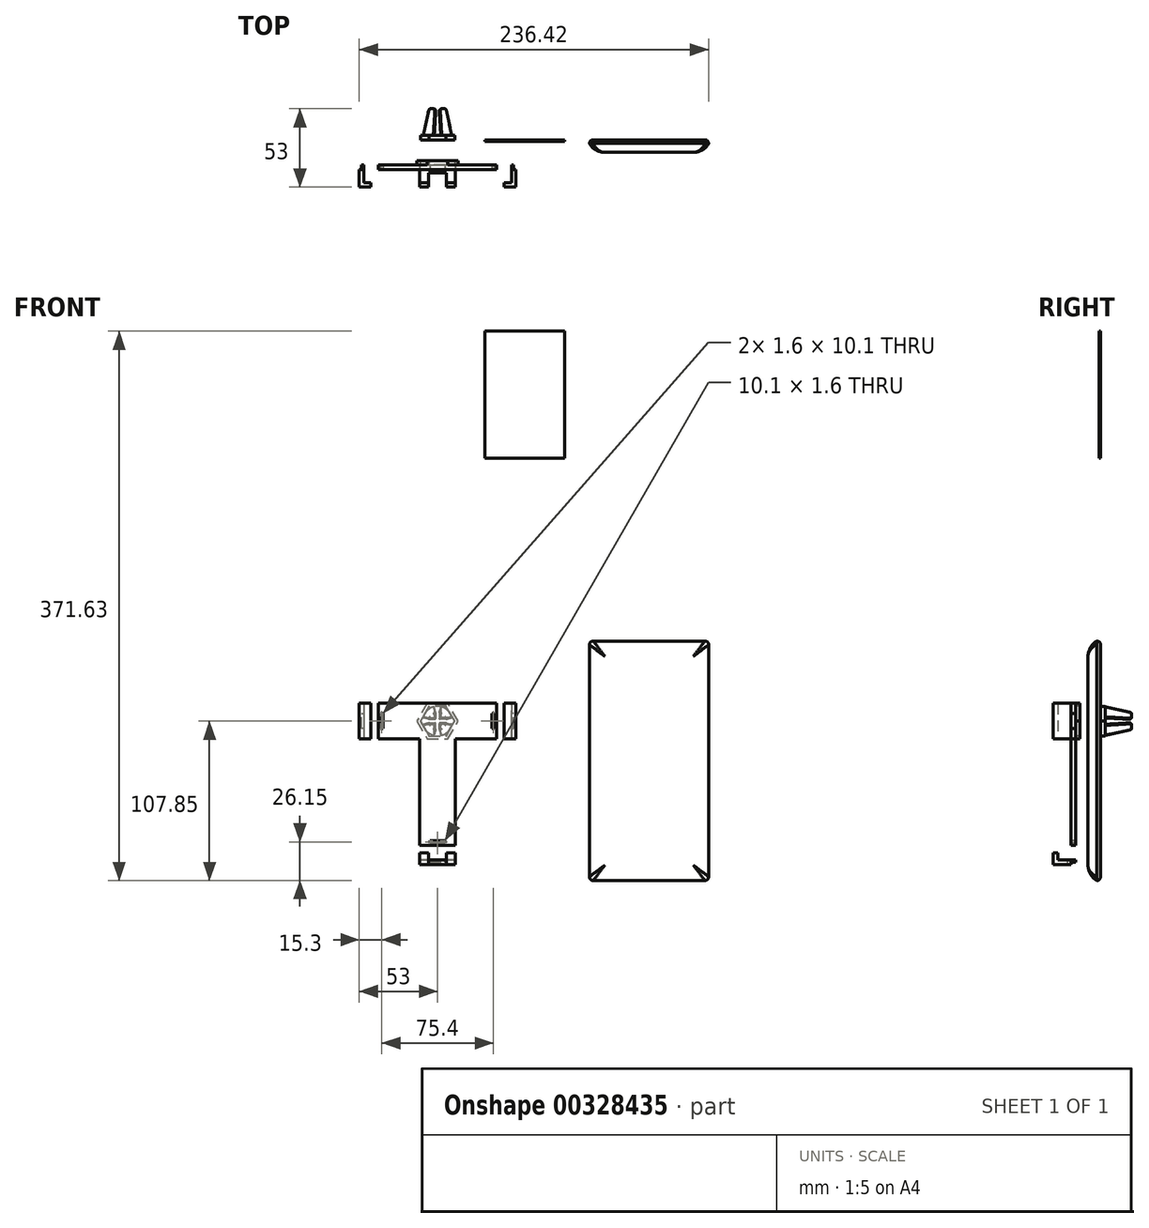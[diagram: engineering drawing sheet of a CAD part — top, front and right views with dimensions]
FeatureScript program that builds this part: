
annotation { "Feature Type Name" : "Feature", "Feature Type Description" : "" }
export const myFeature = defineFeature(function(context is Context, id is Id, definition is map)
    precondition{}
    {
        {
            assignVariable(context, id + "F0", {"name" : "depth_phone", "anyValue" : 8.5});
        }
        {
            var Q0;
            Q0=qCreatedBy(makeId("Front.planeOp"),FACE);
            var sketch = newSketch(context, id + "F1", { "sketchPlane" : qUnion([Q0])});
            skCircle(sketch, "E0", {"center": v(0, 0) * mm, "radius": 10 * mm});
            skSolve(sketch);
        }
        {
            var Q0;
            Q0=qSketchRegion(id+"F1",true);
            extrude(context, id + "F2", {"entities" : qUnion([Q0]), "oppositeDirection" : true, "depth" : 3 * mm});
        }
        {
            var Q0;
            Q0=makeQuery(id+"F2.opExtrude","CAP_FACE",FACE,{"disambiguationData":[OSD([sQuery(id+"F1.wireOp",EDGE,"E0")])],"isStart":false});
            var sketch = newSketch(context, id + "F3", { "sketchPlane" : qUnion([Q0])});
            skLineSegment(sketch, "E1.top", {"start": v(-9.75, 2.2) * mm, "end": v(-2.2, 2.2) * mm});
            skLineSegment(sketch, "E1.right", {"start": v(-2.2, 9.75) * mm, "end": v(-2.2, 2.2) * mm});
            skArc(sketch, "E2", {"start": v(-2.2, 9.75) * mm, "mid": v(-7.07, 7.07) * mm, "end": v(-9.75, 2.2) * mm});
            skLineSegment(sketch, "E3.1.0", {"start": v(-9.75, -2.2) * mm, "end": v(-2.2, -2.2) * mm});
            skLineSegment(sketch, "E3.1.1", {"start": v(-2.2, -9.75) * mm, "end": v(-2.2, -2.2) * mm});
            skArc(sketch, "E3.1.2", {"start": v(-9.75, -2.2) * mm, "mid": v(-7.07, -7.07) * mm, "end": v(-2.2, -9.75) * mm});
            skLineSegment(sketch, "E3.2.0", {"start": v(2.2, -9.75) * mm, "end": v(2.2, -2.2) * mm});
            skLineSegment(sketch, "E3.2.1", {"start": v(9.75, -2.2) * mm, "end": v(2.2, -2.2) * mm});
            skArc(sketch, "E3.2.2", {"start": v(2.2, -9.75) * mm, "mid": v(7.07, -7.07) * mm, "end": v(9.75, -2.2) * mm});
            skLineSegment(sketch, "E4.2.3.0", {"start": v(9.75, 2.2) * mm, "end": v(2.2, 2.2) * mm});
            skLineSegment(sketch, "E4.3.3.0", {"start": v(2.2, 9.75) * mm, "end": v(2.2, 2.2) * mm});
            skArc(sketch, "E4.6.3.0", {"start": v(9.75, 2.2) * mm, "mid": v(7.07, 7.07) * mm, "end": v(2.2, 9.75) * mm});
            skSolve(sketch);
        }
        {
            var Q0;
            Q0=makeQuery(id+"F3.imprint","IMPRINT",FACE,{"disambiguationData":[TD([[makeQuery(id+"F3.imprint","IMPRINT",EDGE,{"derivedFrom":sQuery(id+"F3.wireOp",EDGE,"E1.top")}),-1.0]])]});
            cPlane(context, id + "F4", {"entities" : qUnion([Q0]), "cplaneType" : CPlaneType.OFFSET, "offset" : 18 * mm, "width" : 150 * mm, "height" : 150 * mm});
        }
        {
            var Q0;
            Q0=qCreatedBy(id+"F4.planeOp",FACE);
            var sketch = newSketch(context, id + "F5", { "sketchPlane" : qUnion([Q0])});
            skLineSegment(sketch, "E5.top", {"start": v(-5.9, 1.1) * mm, "end": v(-1.1, 1.1) * mm});
            skLineSegment(sketch, "E5.right", {"start": v(-1.11, 5.9) * mm, "end": v(-1.11, 1.1) * mm});
            skArc(sketch, "E6", {"start": v(-1.11, 5.9) * mm, "mid": v(-4.24, 4.24) * mm, "end": v(-5.9, 1.1) * mm});
            skLineSegment(sketch, "E7.1.0", {"start": v(-5.9, -1.1) * mm, "end": v(-1.1, -1.1) * mm});
            skLineSegment(sketch, "E7.1.1", {"start": v(-1.1, -5.9) * mm, "end": v(-1.11, -1.1) * mm});
            skArc(sketch, "E7.1.2", {"start": v(-5.9, -1.1) * mm, "mid": v(-4.24, -4.24) * mm, "end": v(-1.1, -5.9) * mm});
            skLineSegment(sketch, "E7.2.0", {"start": v(1.1, -5.9) * mm, "end": v(1.1, -1.1) * mm});
            skLineSegment(sketch, "E7.2.1", {"start": v(5.9, -1.1) * mm, "end": v(1.1, -1.11) * mm});
            skArc(sketch, "E7.2.2", {"start": v(1.1, -5.9) * mm, "mid": v(4.24, -4.24) * mm, "end": v(5.9, -1.1) * mm});
            skLineSegment(sketch, "E7.3.0", {"start": v(5.9, 1.1) * mm, "end": v(1.1, 1.1) * mm});
            skLineSegment(sketch, "E7.3.1", {"start": v(1.1, 5.9) * mm, "end": v(1.11, 1.1) * mm});
            skArc(sketch, "E7.3.2", {"start": v(5.9, 1.11) * mm, "mid": v(4.24, 4.24) * mm, "end": v(1.1, 5.9) * mm});
            skSolve(sketch);
        }
        {
            var Q1;
            Q1=makeQuery(id+"F5.imprint","IMPRINT",FACE,{"disambiguationData":[TD([[makeQuery(id+"F5.imprint","IMPRINT",EDGE,{"derivedFrom":sQuery(id+"F5.wireOp",EDGE,"E5.top")}),1.0]])]});
            var Q2;
            Q2=makeQuery(id+"F3.imprint","IMPRINT",FACE,{"disambiguationData":[TD([[makeQuery(id+"F3.imprint","IMPRINT",EDGE,{"derivedFrom":sQuery(id+"F3.wireOp",EDGE,"E1.top")}),1.0]])]});
            loft(context, id + "F6", {"operationType" : NewBodyOperationType.ADD, "sheetProfilesArray" : [{ "sheetProfileEntities" : qUnion([Q1]) }, { "sheetProfileEntities" : qUnion([Q2]) }]});
        }
        {
            var Q1;
            Q1=makeQuery(id+"F3.imprint","IMPRINT",FACE,{"disambiguationData":[TD([[makeQuery(id+"F3.imprint","IMPRINT",EDGE,{"derivedFrom":sQuery(id+"F3.wireOp",EDGE,"E4.2.3.0")}),-1.0]])]});
            var Q2;
            Q2=makeQuery(id+"F5.imprint","IMPRINT",FACE,{"disambiguationData":[TD([[makeQuery(id+"F5.imprint","IMPRINT",EDGE,{"derivedFrom":sQuery(id+"F5.wireOp",EDGE,"E7.3.0")}),-1.0]])]});
            loft(context, id + "F7", {"operationType" : NewBodyOperationType.ADD, "sheetProfilesArray" : [{ "sheetProfileEntities" : qUnion([Q1]) }, { "sheetProfileEntities" : qUnion([Q2]) }]});
        }
        {
            var Q1;
            Q1=makeQuery(id+"F3.imprint","IMPRINT",FACE,{"disambiguationData":[TD([[makeQuery(id+"F3.imprint","IMPRINT",EDGE,{"derivedFrom":sQuery(id+"F3.wireOp",EDGE,"E3.1.0")}),-1.0]])]});
            var Q2;
            Q2=makeQuery(id+"F5.imprint","IMPRINT",FACE,{"disambiguationData":[TD([[makeQuery(id+"F5.imprint","IMPRINT",EDGE,{"derivedFrom":sQuery(id+"F5.wireOp",EDGE,"E7.1.0")}),-1.0]])]});
            loft(context, id + "F8", {"operationType" : NewBodyOperationType.ADD, "sheetProfilesArray" : [{ "sheetProfileEntities" : qUnion([Q1]) }, { "sheetProfileEntities" : qUnion([Q2]) }]});
        }
        {
            var Q1;
            Q1=makeQuery(id+"F3.imprint","IMPRINT",FACE,{"disambiguationData":[TD([[makeQuery(id+"F3.imprint","IMPRINT",EDGE,{"derivedFrom":sQuery(id+"F3.wireOp",EDGE,"E3.2.0")}),-1.0]])]});
            var Q2;
            Q2=makeQuery(id+"F5.imprint","IMPRINT",FACE,{"disambiguationData":[TD([[makeQuery(id+"F5.imprint","IMPRINT",EDGE,{"derivedFrom":sQuery(id+"F5.wireOp",EDGE,"E7.2.0")}),-1.0]])]});
            loft(context, id + "F9", {"operationType" : NewBodyOperationType.ADD, "sheetProfilesArray" : [{ "sheetProfileEntities" : qUnion([Q1]) }, { "sheetProfileEntities" : qUnion([Q2]) }]});
        }
        {
            var Q0;
            {var subQ0=sQuery(id+"F5.wireOp",EDGE,"E6");var subQ1=sQuery(id+"F5.wireOp",EDGE,"E5.right");var subQ2=sQuery(id+"F5.wireOp",EDGE,"E5.top");Q0=makeQuery(id+"F6.opLoft","MID_CAP_EDGE",EDGE,{"disambiguationData":[OSD([subQ2,subQ1,subQ0]),TDD([makeQuery(id+"F5.imprint","INTERSECT",VERTEX,{"derivedFrom":[subQ2,subQ0]}),makeQuery(id+"F5.imprint","INTERSECT",VERTEX,{"derivedFrom":[subQ1,subQ0]}),makeQuery(id+"F5.imprint","IMPRINT",EDGE,{"derivedFrom":subQ0})])],"capPos":0.0});}
            var Q1;
            Q1=makeQuery(id+"F6.opLoft","SWEPT_EDGE",EDGE,{"disambiguationData":[OSD([sQuery(id+"F3.wireOp",EDGE,"E1.right"),sQuery(id+"F3.wireOp",EDGE,"E2"),sQuery(id+"F5.wireOp",EDGE,"E5.right"),sQuery(id+"F5.wireOp",EDGE,"E6")])]});
            var Q2;
            Q2=makeQuery(id+"F6.opLoft","SWEPT_EDGE",EDGE,{"disambiguationData":[OSD([sQuery(id+"F3.wireOp",EDGE,"E1.top"),sQuery(id+"F3.wireOp",EDGE,"E1.right"),sQuery(id+"F5.wireOp",EDGE,"E5.top"),sQuery(id+"F5.wireOp",EDGE,"E5.right")])]});
            var Q3;
            Q3=makeQuery(id+"F6.opLoft","SWEPT_EDGE",EDGE,{"disambiguationData":[OSD([sQuery(id+"F3.wireOp",EDGE,"E1.top"),sQuery(id+"F3.wireOp",EDGE,"E2"),sQuery(id+"F5.wireOp",EDGE,"E5.top"),sQuery(id+"F5.wireOp",EDGE,"E6")])]});
            var Q4;
            {var subQ0=sQuery(id+"F5.wireOp",EDGE,"E7.1.2");var subQ1=sQuery(id+"F5.wireOp",EDGE,"E7.1.1");var subQ2=sQuery(id+"F5.wireOp",EDGE,"E7.1.0");Q4=makeQuery(id+"F8.opLoft","MID_CAP_EDGE",EDGE,{"disambiguationData":[OSD([subQ2,subQ1,subQ0]),TDD([makeQuery(id+"F5.imprint","INTERSECT",VERTEX,{"derivedFrom":[subQ2,subQ0]}),makeQuery(id+"F5.imprint","INTERSECT",VERTEX,{"derivedFrom":[subQ1,subQ0]}),makeQuery(id+"F5.imprint","IMPRINT",EDGE,{"derivedFrom":subQ0})])],"capPos":1.0});}
            var Q5;
            Q5=makeQuery(id+"F8.opLoft","SWEPT_EDGE",EDGE,{"disambiguationData":[OSD([sQuery(id+"F3.wireOp",EDGE,"E3.1.0"),sQuery(id+"F3.wireOp",EDGE,"E3.1.2"),sQuery(id+"F5.wireOp",EDGE,"E7.1.0"),sQuery(id+"F5.wireOp",EDGE,"E7.1.2")])]});
            var Q6;
            Q6=makeQuery(id+"F8.opLoft","SWEPT_EDGE",EDGE,{"disambiguationData":[OSD([sQuery(id+"F3.wireOp",EDGE,"E3.1.0"),sQuery(id+"F3.wireOp",EDGE,"E3.1.1"),sQuery(id+"F5.wireOp",EDGE,"E7.1.0"),sQuery(id+"F5.wireOp",EDGE,"E7.1.1")])]});
            var Q7;
            Q7=makeQuery(id+"F8.opLoft","SWEPT_EDGE",EDGE,{"disambiguationData":[OSD([sQuery(id+"F3.wireOp",EDGE,"E3.1.1"),sQuery(id+"F3.wireOp",EDGE,"E3.1.2"),sQuery(id+"F5.wireOp",EDGE,"E7.1.1"),sQuery(id+"F5.wireOp",EDGE,"E7.1.2")])]});
            var Q8;
            {var subQ0=sQuery(id+"F5.wireOp",EDGE,"E7.2.2");var subQ1=sQuery(id+"F5.wireOp",EDGE,"E7.2.1");var subQ2=sQuery(id+"F5.wireOp",EDGE,"E7.2.0");Q8=makeQuery(id+"F9.opLoft","MID_CAP_EDGE",EDGE,{"disambiguationData":[OSD([subQ2,subQ1,subQ0]),TDD([makeQuery(id+"F5.imprint","INTERSECT",VERTEX,{"derivedFrom":[subQ2,subQ0]}),makeQuery(id+"F5.imprint","INTERSECT",VERTEX,{"derivedFrom":[subQ1,subQ0]}),makeQuery(id+"F5.imprint","IMPRINT",EDGE,{"derivedFrom":subQ0})])],"capPos":1.0});}
            var Q9;
            Q9=makeQuery(id+"F9.opLoft","SWEPT_EDGE",EDGE,{"disambiguationData":[OSD([sQuery(id+"F3.wireOp",EDGE,"E3.2.0"),sQuery(id+"F3.wireOp",EDGE,"E3.2.2"),sQuery(id+"F5.wireOp",EDGE,"E7.2.0"),sQuery(id+"F5.wireOp",EDGE,"E7.2.2")])]});
            var Q10;
            Q10=makeQuery(id+"F9.opLoft","SWEPT_EDGE",EDGE,{"disambiguationData":[OSD([sQuery(id+"F3.wireOp",EDGE,"E3.2.1"),sQuery(id+"F3.wireOp",EDGE,"E3.2.2"),sQuery(id+"F5.wireOp",EDGE,"E7.2.1"),sQuery(id+"F5.wireOp",EDGE,"E7.2.2")])]});
            var Q11;
            Q11=makeQuery(id+"F9.opLoft","SWEPT_EDGE",EDGE,{"disambiguationData":[OSD([sQuery(id+"F3.wireOp",EDGE,"E3.2.0"),sQuery(id+"F3.wireOp",EDGE,"E3.2.1"),sQuery(id+"F5.wireOp",EDGE,"E7.2.0"),sQuery(id+"F5.wireOp",EDGE,"E7.2.1")])]});
            var Q12;
            {var subQ0=sQuery(id+"F5.wireOp",EDGE,"E7.3.2");var subQ1=sQuery(id+"F5.wireOp",EDGE,"E7.3.1");var subQ2=sQuery(id+"F5.wireOp",EDGE,"E7.3.0");Q12=makeQuery(id+"F7.opLoft","MID_CAP_EDGE",EDGE,{"disambiguationData":[OSD([subQ2,subQ1,subQ0]),TDD([makeQuery(id+"F5.imprint","INTERSECT",VERTEX,{"derivedFrom":[subQ2,subQ0]}),makeQuery(id+"F5.imprint","INTERSECT",VERTEX,{"derivedFrom":[subQ1,subQ0]}),makeQuery(id+"F5.imprint","IMPRINT",EDGE,{"derivedFrom":subQ0})])],"capPos":1.0});}
            var Q13;
            Q13=makeQuery(id+"F7.opLoft","SWEPT_EDGE",EDGE,{"disambiguationData":[OSD([sQuery(id+"F3.wireOp",EDGE,"E4.2.3.0"),sQuery(id+"F3.wireOp",EDGE,"E4.3.3.0"),sQuery(id+"F5.wireOp",EDGE,"E7.3.0"),sQuery(id+"F5.wireOp",EDGE,"E7.3.1")])]});
            var Q14;
            Q14=makeQuery(id+"F7.opLoft","SWEPT_EDGE",EDGE,{"disambiguationData":[OSD([sQuery(id+"F3.wireOp",EDGE,"E4.2.3.0"),sQuery(id+"F3.wireOp",EDGE,"E4.6.3.0"),sQuery(id+"F5.wireOp",EDGE,"E7.3.0"),sQuery(id+"F5.wireOp",EDGE,"E7.3.2")])]});
            var Q15;
            Q15=makeQuery(id+"F7.opLoft","SWEPT_EDGE",EDGE,{"disambiguationData":[OSD([sQuery(id+"F3.wireOp",EDGE,"E4.3.3.0"),sQuery(id+"F3.wireOp",EDGE,"E4.6.3.0"),sQuery(id+"F5.wireOp",EDGE,"E7.3.1"),sQuery(id+"F5.wireOp",EDGE,"E7.3.2")])]});
            fillet(context, id + "F10", {"entities" : qUnion([Q0, Q1, Q2, Q3, Q4, Q5, Q6, Q7, Q8, Q9, Q10, Q11, Q12, Q13, Q14, Q15]), "radius" : .5 * mm, "tangentPropagation" : true, "allowEdgeOverflow" : false});
        }
        {
            var Q0;
            Q0=qCreatedBy(makeId("Front.planeOp"),FACE);
            var sketch = newSketch(context, id + "F11", { "sketchPlane" : qUnion([Q0])});
            skLineSegment(sketch, "E8.bottom", {"start": v(86.03, 177.78) * mm, "end": v(32.03, 177.78) * mm});
            skLineSegment(sketch, "E8.top", {"start": v(86.03, 263.78) * mm, "end": v(32.03, 263.78) * mm});
            skLineSegment(sketch, "E8.left", {"start": v(86.03, 177.78) * mm, "end": v(86.03, 263.78) * mm});
            skLineSegment(sketch, "E8.right", {"start": v(32.03, 177.78) * mm, "end": v(32.03, 263.78) * mm});
            skSolve(sketch);
        }
        {
            var Q0;
            Q0=makeQuery(id+"F11.imprint","IMPRINT",FACE,{"disambiguationData":[TD([[makeQuery(id+"F11.imprint","IMPRINT",EDGE,{"derivedFrom":sQuery(id+"F11.wireOp",EDGE,"E8.bottom")}),-1.0]])]});
            extrude(context, id + "F12", {"entities" : qUnion([Q0]), "depth" : 1 * mm});
        }
        {
            var Q0;
            {var subQ0=sQuery(id+"F5.wireOp",EDGE,"E5.right");var subQ1=sQuery(id+"F5.wireOp",EDGE,"E6");var subQ2=sQuery(id+"F5.wireOp",EDGE,"E5.top");Q0=makeQuery(id+"F6.opLoft","MID_CAP_EDGE",EDGE,{"disambiguationData":[OSD([subQ2,subQ0,subQ1]),TDD([makeQuery(id+"F5.imprint","INTERSECT",VERTEX,{"derivedFrom":[subQ2,subQ0]}),makeQuery(id+"F5.imprint","INTERSECT",VERTEX,{"derivedFrom":[subQ0,subQ1]}),makeQuery(id+"F5.imprint","IMPRINT",EDGE,{"derivedFrom":subQ0})])],"capPos":0.0});}
            var Q1;
            {var subQ0=sQuery(id+"F5.wireOp",EDGE,"E5.top");var subQ1=sQuery(id+"F5.wireOp",EDGE,"E5.right");var subQ2=sQuery(id+"F5.wireOp",EDGE,"E6");Q1=makeQuery(id+"F6.opLoft","MID_CAP_EDGE",EDGE,{"disambiguationData":[OSD([subQ0,subQ1,subQ2]),TDD([makeQuery(id+"F5.imprint","INTERSECT",VERTEX,{"derivedFrom":[subQ0,subQ2]}),makeQuery(id+"F5.imprint","INTERSECT",VERTEX,{"derivedFrom":[subQ0,subQ1]}),makeQuery(id+"F5.imprint","IMPRINT",EDGE,{"derivedFrom":subQ0})])],"capPos":0.0});}
            var Q2;
            {var subQ0=sQuery(id+"F5.wireOp",EDGE,"E7.1.0");var subQ1=sQuery(id+"F5.wireOp",EDGE,"E7.1.1");var subQ2=sQuery(id+"F5.wireOp",EDGE,"E7.1.2");Q2=makeQuery(id+"F8.opLoft","MID_CAP_EDGE",EDGE,{"disambiguationData":[OSD([subQ0,subQ1,subQ2]),TDD([makeQuery(id+"F5.imprint","INTERSECT",VERTEX,{"derivedFrom":[subQ0,subQ2]}),makeQuery(id+"F5.imprint","INTERSECT",VERTEX,{"derivedFrom":[subQ0,subQ1]}),makeQuery(id+"F5.imprint","IMPRINT",EDGE,{"derivedFrom":subQ0})])],"capPos":1.0});}
            var Q3;
            {var subQ0=sQuery(id+"F5.wireOp",EDGE,"E7.1.1");var subQ1=sQuery(id+"F5.wireOp",EDGE,"E7.1.2");var subQ2=sQuery(id+"F5.wireOp",EDGE,"E7.1.0");Q3=makeQuery(id+"F8.opLoft","MID_CAP_EDGE",EDGE,{"disambiguationData":[OSD([subQ2,subQ0,subQ1]),TDD([makeQuery(id+"F5.imprint","INTERSECT",VERTEX,{"derivedFrom":[subQ2,subQ0]}),makeQuery(id+"F5.imprint","INTERSECT",VERTEX,{"derivedFrom":[subQ0,subQ1]}),makeQuery(id+"F5.imprint","IMPRINT",EDGE,{"derivedFrom":subQ0})])],"capPos":1.0});}
            var Q4;
            {var subQ0=sQuery(id+"F5.wireOp",EDGE,"E7.2.0");var subQ1=sQuery(id+"F5.wireOp",EDGE,"E7.2.1");var subQ2=sQuery(id+"F5.wireOp",EDGE,"E7.2.2");Q4=makeQuery(id+"F9.opLoft","MID_CAP_EDGE",EDGE,{"disambiguationData":[OSD([subQ0,subQ1,subQ2]),TDD([makeQuery(id+"F5.imprint","INTERSECT",VERTEX,{"derivedFrom":[subQ0,subQ2]}),makeQuery(id+"F5.imprint","INTERSECT",VERTEX,{"derivedFrom":[subQ0,subQ1]}),makeQuery(id+"F5.imprint","IMPRINT",EDGE,{"derivedFrom":subQ0})])],"capPos":1.0});}
            var Q5;
            {var subQ0=sQuery(id+"F5.wireOp",EDGE,"E7.2.1");var subQ1=sQuery(id+"F5.wireOp",EDGE,"E7.2.2");var subQ2=sQuery(id+"F5.wireOp",EDGE,"E7.2.0");Q5=makeQuery(id+"F9.opLoft","MID_CAP_EDGE",EDGE,{"disambiguationData":[OSD([subQ2,subQ0,subQ1]),TDD([makeQuery(id+"F5.imprint","INTERSECT",VERTEX,{"derivedFrom":[subQ2,subQ0]}),makeQuery(id+"F5.imprint","INTERSECT",VERTEX,{"derivedFrom":[subQ0,subQ1]}),makeQuery(id+"F5.imprint","IMPRINT",EDGE,{"derivedFrom":subQ0})])],"capPos":1.0});}
            var Q6;
            {var subQ0=sQuery(id+"F5.wireOp",EDGE,"E7.3.0");var subQ1=sQuery(id+"F5.wireOp",EDGE,"E7.3.1");var subQ2=sQuery(id+"F5.wireOp",EDGE,"E7.3.2");Q6=makeQuery(id+"F7.opLoft","MID_CAP_EDGE",EDGE,{"disambiguationData":[OSD([subQ0,subQ1,subQ2]),TDD([makeQuery(id+"F5.imprint","INTERSECT",VERTEX,{"derivedFrom":[subQ0,subQ2]}),makeQuery(id+"F5.imprint","INTERSECT",VERTEX,{"derivedFrom":[subQ0,subQ1]}),makeQuery(id+"F5.imprint","IMPRINT",EDGE,{"derivedFrom":subQ0})])],"capPos":1.0});}
            var Q7;
            {var subQ0=sQuery(id+"F5.wireOp",EDGE,"E7.3.1");var subQ1=sQuery(id+"F5.wireOp",EDGE,"E7.3.2");var subQ2=sQuery(id+"F5.wireOp",EDGE,"E7.3.0");Q7=makeQuery(id+"F7.opLoft","MID_CAP_EDGE",EDGE,{"disambiguationData":[OSD([subQ2,subQ0,subQ1]),TDD([makeQuery(id+"F5.imprint","INTERSECT",VERTEX,{"derivedFrom":[subQ2,subQ0]}),makeQuery(id+"F5.imprint","INTERSECT",VERTEX,{"derivedFrom":[subQ0,subQ1]}),makeQuery(id+"F5.imprint","IMPRINT",EDGE,{"derivedFrom":subQ0})])],"capPos":1.0});}
            fillet(context, id + "F13", {"entities" : qUnion([Q0, Q1, Q2, Q3, Q4, Q5, Q6, Q7]), "radius" : 1.5 * mm, "tangentPropagation" : true, "allowEdgeOverflow" : false});
        }
        {
            var Q0;
            Q0=qCreatedBy(makeId("Front.planeOp"),FACE);
            var sketch = newSketch(context, id + "F14", { "sketchPlane" : qUnion([Q0])});
            skLineSegment(sketch, "E9.bottom", {"start": v(102.82, 54.15) * mm, "end": v(183.42, 54.15) * mm});
            skLineSegment(sketch, "E9.top", {"start": v(102.82, -107.85) * mm, "end": v(183.42, -107.85) * mm});
            skLineSegment(sketch, "E9.left", {"start": v(102.82, 54.15) * mm, "end": v(102.82, -107.85) * mm});
            skLineSegment(sketch, "E9.right", {"start": v(183.42, 54.15) * mm, "end": v(183.42, -107.85) * mm});
            skSolve(sketch);
        }
        {
            var Q0;
            Q0=qSketchRegion(id+"F14",true);
            extrude(context, id + "F15", {"entities" : qUnion([Q0]), "depth" : (getVariable(context, 'depth_phone')) * mm});
        }
        {
            var Q0;
            Q0=makeQuery(id+"F15.opExtrude","SWEPT_EDGE",EDGE,{"disambiguationData":[OSD([sQuery(id+"F14.wireOp",EDGE,"E9.bottom"),sQuery(id+"F14.wireOp",EDGE,"E9.left")])]});
            var Q1;
            Q1=makeQuery(id+"F15.opExtrude","SWEPT_EDGE",EDGE,{"disambiguationData":[OSD([sQuery(id+"F14.wireOp",EDGE,"E9.bottom"),sQuery(id+"F14.wireOp",EDGE,"E9.right")])]});
            var Q2;
            Q2=makeQuery(id+"F15.opExtrude","SWEPT_EDGE",EDGE,{"disambiguationData":[OSD([sQuery(id+"F14.wireOp",EDGE,"E9.top"),sQuery(id+"F14.wireOp",EDGE,"E9.right")])]});
            var Q3;
            Q3=makeQuery(id+"F15.opExtrude","SWEPT_EDGE",EDGE,{"disambiguationData":[OSD([sQuery(id+"F14.wireOp",EDGE,"E9.top"),sQuery(id+"F14.wireOp",EDGE,"E9.left")])]});
            fillet(context, id + "F16", {"entities" : qUnion([Q0, Q1, Q2, Q3]), "radius" : 2.5 * mm, "tangentPropagation" : true, "allowEdgeOverflow" : false});
        }
        {
            var Q0;
            Q0=makeQuery(id+"F15.opExtrude","CAP_EDGE",EDGE,{"disambiguationData":[OSD([sQuery(id+"F14.wireOp",EDGE,"E9.right")])],"isStart":true});
            var Q1;
            Q1=makeQuery(id+"F15.opExtrude","CAP_EDGE",EDGE,{"disambiguationData":[OSD([sQuery(id+"F14.wireOp",EDGE,"E9.bottom")])],"isStart":true});
            var Q2;
            Q2=makeQuery(id+"F15.opExtrude","CAP_EDGE",EDGE,{"disambiguationData":[OSD([sQuery(id+"F14.wireOp",EDGE,"E9.left")])],"isStart":true});
            var Q3;
            Q3=makeQuery(id+"F15.opExtrude","CAP_EDGE",EDGE,{"disambiguationData":[OSD([sQuery(id+"F14.wireOp",EDGE,"E9.top")])],"isStart":true});
            fillet(context, id + "F17", {"entities" : qUnion([Q0, Q1, Q2, Q3]), "radius" : 2.5 * mm, "tangentPropagation" : true, "allowEdgeOverflow" : false});
        }
        {
            var Q0;
            Q0=makeQuery(id+"F15.opExtrude","CAP_EDGE",EDGE,{"disambiguationData":[OSD([sQuery(id+"F14.wireOp",EDGE,"E9.right")])],"isStart":false});
            var Q1;
            Q1=makeQuery(id+"F15.opExtrude","CAP_EDGE",EDGE,{"disambiguationData":[OSD([sQuery(id+"F14.wireOp",EDGE,"E9.bottom")])],"isStart":false});
            var Q2;
            Q2=makeQuery(id+"F15.opExtrude","CAP_EDGE",EDGE,{"disambiguationData":[OSD([sQuery(id+"F14.wireOp",EDGE,"E9.left")])],"isStart":false});
            var Q3;
            Q3=makeQuery(id+"F15.opExtrude","CAP_EDGE",EDGE,{"disambiguationData":[OSD([sQuery(id+"F14.wireOp",EDGE,"E9.top")])],"isStart":false});
            fillet(context, id + "F18", {"entities" : qUnion([Q0, Q1, Q2, Q3]), "radius" : 12 * mm, "tangentPropagation" : true, "allowEdgeOverflow" : false});
        }
        {
            var Q0;
            Q0=qCreatedBy(makeId("Front.planeOp"),FACE);
            cPlane(context, id + "F19", {"entities" : qUnion([Q0]), "cplaneType" : CPlaneType.OFFSET, "offset" : 20 * mm, "width" : 150 * mm, "height" : 150 * mm});
        }
        {
            var Q0;
            Q0=qCreatedBy(id+"F19.planeOp",FACE);
            var sketch = newSketch(context, id + "F20", { "sketchPlane" : qUnion([Q0])});
            skLineSegment(sketch, "E10.bottom", {"start": v(-12, -84) * mm, "end": v(12, -84) * mm});
            skLineSegment(sketch, "E10.top", {"start": v(-12, 0) * mm, "end": v(12, 0) * mm});
            skLineSegment(sketch, "E10.left", {"start": v(-12, -84) * mm, "end": v(-12, 0) * mm});
            skLineSegment(sketch, "E10.right", {"start": v(12, -84) * mm, "end": v(12, 0) * mm});
            skSolve(sketch);
        }
        {
            var Q0;
            Q0=qSketchRegion(id+"F20",true);
            extrude(context, id + "F21", {"entities" : qUnion([Q0]), "operationType" : NewBodyOperationType.ADD, "oppositeDirection" : true, "depth" : 3 * mm});
        }
        {
            var Q0;
            Q0=makeQuery(id+"F21.opExtrude","SWEPT_FACE",FACE,{"disambiguationData":[OSD([sQuery(id+"F20.wireOp",EDGE,"E10.bottom")])]});
            cPlane(context, id + "F22", {"entities" : qUnion([Q0]), "cplaneType" : CPlaneType.OFFSET, "offset" : 10 * mm, "width" : 150 * mm, "height" : 150 * mm});
        }
        {
            var Q0;
            Q0=qCreatedBy(id+"F22.planeOp",FACE);
            var sketch = newSketch(context, id + "F23", { "sketchPlane" : qUnion([Q0])});
            skLineSegment(sketch, "E11.bottom", {"start": v(12, 17) * mm, "end": v(-12, 17) * mm});
            skLineSegment(sketch, "E11.top", {"start": v(12, 29) * mm, "end": v(-12, 29) * mm});
            skLineSegment(sketch, "E11.left", {"start": v(12, 17) * mm, "end": v(12, 29) * mm});
            skLineSegment(sketch, "E11.right", {"start": v(-12, 17) * mm, "end": v(-12, 29) * mm});
            skSolve(sketch);
        }
        {
            var Q0;
            Q0=qSketchRegion(id+"F23",true);
            extrude(context, id + "F24", {"entities" : qUnion([Q0]), "operationType" : NewBodyOperationType.ADD, "depth" : 3 * mm});
        }
        {
            var Q0;
            Q0=qCreatedBy(id+"F19.planeOp",FACE);
            var sketch = newSketch(context, id + "F25", { "sketchPlane" : qUnion([Q0])});
            skLineSegment(sketch, "E12.bottom", {"start": v(40, 12) * mm, "end": v(-40, 12) * mm});
            skLineSegment(sketch, "E12.top", {"start": v(40, -12) * mm, "end": v(-40, -12) * mm});
            skLineSegment(sketch, "E12.left", {"start": v(40, 12) * mm, "end": v(40, -12) * mm});
            skLineSegment(sketch, "E12.right", {"start": v(-40, 12) * mm, "end": v(-40, -12) * mm});
            skLineSegment(sketch, "E13", {"start": v(40, 0) * mm, "end": v(-40, 0) * mm, "construction": true});
            skLineSegment(sketch, "E14", {"start": v(0, -12) * mm, "end": v(0, 12) * mm, "construction": true});
            skPoint(sketch, "E15", {"position": v(0, 0) * mm});
            skSolve(sketch);
        }
        {
            var Q0;
            Q0=makeQuery(id+"F25.imprint","IMPRINT",FACE,{"disambiguationData":[TD([[makeQuery(id+"F25.imprint","IMPRINT",EDGE,{"derivedFrom":sQuery(id+"F25.wireOp",EDGE,"E12.bottom")}),1.0]])]});
            extrude(context, id + "F26", {"entities" : qUnion([Q0]), "operationType" : NewBodyOperationType.ADD, "oppositeDirection" : true, "depth" : 3 * mm});
        }
        {
            var Q0;
            Q0=makeQuery(id+"F26.opExtrude","SWEPT_FACE",FACE,{"disambiguationData":[OSD([sQuery(id+"F25.wireOp",EDGE,"E12.right")])]});
            cPlane(context, id + "F27", {"entities" : qUnion([Q0]), "cplaneType" : CPlaneType.OFFSET, "offset" : 10 * mm, "width" : 150 * mm, "height" : 150 * mm});
        }
        {
            var Q0;
            Q0=qCreatedBy(id+"F27.planeOp",FACE);
            var sketch = newSketch(context, id + "F28", { "sketchPlane" : qUnion([Q0])});
            skLineSegment(sketch, "E16.bottom", {"start": v(17, 12) * mm, "end": v(29, 12) * mm});
            skLineSegment(sketch, "E16.top", {"start": v(17, -12) * mm, "end": v(29, -12) * mm});
            skLineSegment(sketch, "E16.left", {"start": v(17, 12) * mm, "end": v(17, -12) * mm});
            skLineSegment(sketch, "E16.right", {"start": v(29, 12) * mm, "end": v(29, -12) * mm});
            skSolve(sketch);
        }
        {
            var Q0;
            Q0=qSketchRegion(id+"F28",true);
            extrude(context, id + "F29", {"entities" : qUnion([Q0]), "operationType" : NewBodyOperationType.ADD, "depth" : 3 * mm});
        }
        {
            var Q0;
            Q0=makeQuery(id+"F26.opExtrude","SWEPT_FACE",FACE,{"disambiguationData":[OSD([sQuery(id+"F25.wireOp",EDGE,"E12.left")])]});
            cPlane(context, id + "F30", {"entities" : qUnion([Q0]), "cplaneType" : CPlaneType.OFFSET, "offset" : 10 * mm, "width" : 150 * mm, "height" : 150 * mm});
        }
        {
            var Q0;
            Q0=qCreatedBy(id+"F30.planeOp",FACE);
            var sketch = newSketch(context, id + "F31", { "sketchPlane" : qUnion([Q0])});
            skLineSegment(sketch, "E17.bottom", {"start": v(-17, -12) * mm, "end": v(-29, -12) * mm});
            skLineSegment(sketch, "E17.top", {"start": v(-17, 12) * mm, "end": v(-29, 12) * mm});
            skLineSegment(sketch, "E17.left", {"start": v(-17, -12) * mm, "end": v(-17, 12) * mm});
            skLineSegment(sketch, "E17.right", {"start": v(-29, -12) * mm, "end": v(-29, 12) * mm});
            skSolve(sketch);
        }
        {
            var Q0;
            Q0=qSketchRegion(id+"F31",true);
            extrude(context, id + "F32", {"entities" : qUnion([Q0]), "operationType" : NewBodyOperationType.ADD, "depth" : 3 * mm});
        }
        {
            var Q0;
            Q0=makeQuery(id+"F24.opExtrude","CAP_FACE",FACE,{"disambiguationData":[OSD([sQuery(id+"F23.wireOp",EDGE,"E11.bottom"),sQuery(id+"F23.wireOp",EDGE,"E11.top"),sQuery(id+"F23.wireOp",EDGE,"E11.left"),sQuery(id+"F23.wireOp",EDGE,"E11.right")])],"isStart":false});
            var sketch = newSketch(context, id + "F33", { "sketchPlane" : qUnion([Q0])});
            skLineSegment(sketch, "E18.bottom", {"start": v(-6, 29) * mm, "end": v(6, 29) * mm});
            skLineSegment(sketch, "E18.top", {"start": v(-6, 20) * mm, "end": v(6, 20) * mm});
            skLineSegment(sketch, "E18.left", {"start": v(-6, 29) * mm, "end": v(-6, 20) * mm});
            skLineSegment(sketch, "E18.right", {"start": v(6, 29) * mm, "end": v(6, 20) * mm});
            skLineSegment(sketch, "E19", {"start": v(0, 20) * mm, "end": v(0, 29) * mm, "construction": true});
            skSolve(sketch);
        }
        {
            var Q0;
            Q0=qSketchRegion(id+"F33",true);
            extrude(context, id + "F34", {"entities" : qUnion([Q0]), "operationType" : NewBodyOperationType.REMOVE, "endBound" : BoundingType.UP_TO_NEXT, "oppositeDirection" : true, "depth" : 25 * mm});
        }
        {
            var Q0;
            Q0=makeQuery(id+"F29.opExtrude","SWEPT_FACE",FACE,{"disambiguationData":[OSD([sQuery(id+"F28.wireOp",EDGE,"E16.right")])]});
            var sketch = newSketch(context, id + "F35", { "sketchPlane" : qUnion([Q0])});
            skLineSegment(sketch, "E20.bottom", {"start": v(-53, -12) * mm, "end": v(-45, -12) * mm});
            skLineSegment(sketch, "E20.top", {"start": v(-53, 12) * mm, "end": v(-45, 12) * mm});
            skLineSegment(sketch, "E20.left", {"start": v(-53, -12) * mm, "end": v(-53, 12) * mm});
            skLineSegment(sketch, "E20.right", {"start": v(-45, -12) * mm, "end": v(-45, 12) * mm});
            skLineSegment(sketch, "E21.bottom", {"start": v(53, -12) * mm, "end": v(45, -12) * mm});
            skLineSegment(sketch, "E21.top", {"start": v(53, 12) * mm, "end": v(45, 12) * mm});
            skLineSegment(sketch, "E21.left", {"start": v(53, -12) * mm, "end": v(53, 12) * mm});
            skLineSegment(sketch, "E21.right", {"start": v(45, -12) * mm, "end": v(45, 12) * mm});
            skLineSegment(sketch, "E22.bottom", {"start": v(-12, -97) * mm, "end": v(-6, -97) * mm});
            skLineSegment(sketch, "E22.top", {"start": v(-12, -89) * mm, "end": v(-6, -89) * mm});
            skLineSegment(sketch, "E22.left", {"start": v(-12, -97) * mm, "end": v(-12, -89) * mm});
            skLineSegment(sketch, "E22.right", {"start": v(-6, -97) * mm, "end": v(-6, -89) * mm});
            skLineSegment(sketch, "E23.bottom", {"start": v(6, -97) * mm, "end": v(12, -97) * mm});
            skLineSegment(sketch, "E23.top", {"start": v(6, -89) * mm, "end": v(12, -89) * mm});
            skLineSegment(sketch, "E23.left", {"start": v(6, -97) * mm, "end": v(6, -89) * mm});
            skLineSegment(sketch, "E23.right", {"start": v(12, -97) * mm, "end": v(12, -89) * mm});
            skSolve(sketch);
        }
        {
            var Q0;
            Q0=qSketchRegion(id+"F35",true);
            extrude(context, id + "F36", {"entities" : qUnion([Q0]), "operationType" : NewBodyOperationType.ADD, "depth" : 3 * mm});
        }
        {
            var Q0;
            Q0=makeQuery(id+"F32.boolean.opBoolean","MERGE",FACE,{"derivedFrom":[makeQuery(id+"F29.boolean.opBoolean","MERGE",FACE,{"derivedFrom":[makeQuery(id+"F26.boolean.opBoolean","MERGE",FACE,{"derivedFrom":[makeQuery(id+"F24.boolean.opBoolean","MERGE",FACE,{"derivedFrom":[makeQuery(id+"F21.opExtrude","CAP_FACE",FACE,{"disambiguationData":[OSD([sQuery(id+"F20.wireOp",EDGE,"E10.bottom"),sQuery(id+"F20.wireOp",EDGE,"E10.top"),sQuery(id+"F20.wireOp",EDGE,"E10.left"),sQuery(id+"F20.wireOp",EDGE,"E10.right")])],"isStart":false}),makeQuery(id+"F24.opExtrude","SWEPT_FACE",FACE,{"disambiguationData":[OSD([sQuery(id+"F23.wireOp",EDGE,"E11.bottom")])]})]}),makeQuery(id+"F26.opExtrude","CAP_FACE",FACE,{"disambiguationData":[OSD([sQuery(id+"F25.wireOp",EDGE,"E12.bottom"),sQuery(id+"F25.wireOp",EDGE,"E12.top"),sQuery(id+"F25.wireOp",EDGE,"E12.left"),sQuery(id+"F25.wireOp",EDGE,"E12.right")])],"isStart":false})]}),makeQuery(id+"F29.opExtrude","SWEPT_FACE",FACE,{"disambiguationData":[OSD([sQuery(id+"F28.wireOp",EDGE,"E16.left")])]})]}),makeQuery(id+"F32.opExtrude","SWEPT_FACE",FACE,{"disambiguationData":[OSD([sQuery(id+"F31.wireOp",EDGE,"E17.left")])]})]});
            var sketch = newSketch(context, id + "F37", { "sketchPlane" : qUnion([Q0])});
            skCircle(sketch, "E24.cCircle", {"center": v(0, 0) * mm, "radius": 10.1 * mm, "construction": true});
            skLineSegment(sketch, "E24.0", {"start": v(11.66, 0) * mm, "end": v(5.83, -10.1) * mm});
            skLineSegment(sketch, "E24.1", {"start": v(5.83, -10.1) * mm, "end": v(-5.83, -10.1) * mm});
            skLineSegment(sketch, "E24.2", {"start": v(-5.83, -10.1) * mm, "end": v(-11.66, 0) * mm});
            skLineSegment(sketch, "E24.3", {"start": v(-11.66, 0) * mm, "end": v(-5.83, 10.1) * mm});
            skLineSegment(sketch, "E24.4", {"start": v(-5.83, 10.1) * mm, "end": v(5.83, 10.1) * mm});
            skLineSegment(sketch, "E24.5", {"start": v(5.83, 10.1) * mm, "end": v(11.66, 0) * mm});
            skPoint(sketch, "E24.0.midPoint", {"position": v(8.75, -5.05) * mm});
            skCircle(sketch, "E25.cCircle", {"center": v(0, 0) * mm, "radius": 12 * mm, "construction": true});
            skLineSegment(sketch, "E25.0", {"start": v(13.86, 0) * mm, "end": v(6.93, -12) * mm});
            skLineSegment(sketch, "E25.1", {"start": v(6.93, -12) * mm, "end": v(-6.93, -12) * mm});
            skLineSegment(sketch, "E25.2", {"start": v(-6.93, -12) * mm, "end": v(-13.86, 0) * mm});
            skLineSegment(sketch, "E25.3", {"start": v(-13.86, 0) * mm, "end": v(-6.93, 12) * mm});
            skLineSegment(sketch, "E25.4", {"start": v(-6.93, 12) * mm, "end": v(6.93, 12) * mm});
            skLineSegment(sketch, "E25.5", {"start": v(6.93, 12) * mm, "end": v(13.86, 0) * mm});
            skPoint(sketch, "E25.0.midPoint", {"position": v(10.4, -6) * mm});
            skSolve(sketch);
        }
        {
            var Q0;
            Q0=qSketchRegion(id+"F37",true);
            extrude(context, id + "F38", {"entities" : qUnion([Q0]), "operationType" : NewBodyOperationType.ADD, "depth" : 3 * mm});
        }
        {
            var Q0;
            Q0=makeQuery(id+"F2.opExtrude","CAP_FACE",FACE,{"disambiguationData":[OSD([sQuery(id+"F1.wireOp",EDGE,"E0")])],"isStart":false});
            var sketch = newSketch(context, id + "F39", { "sketchPlane" : qUnion([Q0])});
            skCircle(sketch, "E26.cCircle", {"center": v(0, 0) * mm, "radius": 10 * mm, "construction": true});
            skLineSegment(sketch, "E26.0", {"start": v(11.55, 0) * mm, "end": v(5.77, -10) * mm});
            skLineSegment(sketch, "E26.1", {"start": v(5.77, -10) * mm, "end": v(-5.77, -10) * mm});
            skLineSegment(sketch, "E26.2", {"start": v(-5.77, -10) * mm, "end": v(-11.55, 0) * mm});
            skLineSegment(sketch, "E26.3", {"start": v(-11.55, 0) * mm, "end": v(-5.77, 10) * mm});
            skLineSegment(sketch, "E26.4", {"start": v(-5.77, 10) * mm, "end": v(5.77, 10) * mm});
            skLineSegment(sketch, "E26.5", {"start": v(5.77, 10) * mm, "end": v(11.55, 0) * mm});
            skPoint(sketch, "E26.0.midPoint", {"position": v(8.66, -5) * mm});
            skSolve(sketch);
        }
        {
            var Q0;
            Q0=qSketchRegion(id+"F39",true);
            extrude(context, id + "F40", {"entities" : qUnion([Q0]), "operationType" : NewBodyOperationType.ADD, "oppositeDirection" : true, "depth" : 3 * mm});
        }
        {
            var Q0;
            Q0=makeQuery(id+"F26.boolean.opBoolean","MERGE",FACE,{"derivedFrom":[makeQuery(id+"F21.opExtrude","CAP_FACE",FACE,{"disambiguationData":[OSD([sQuery(id+"F20.wireOp",EDGE,"E10.bottom"),sQuery(id+"F20.wireOp",EDGE,"E10.top"),sQuery(id+"F20.wireOp",EDGE,"E10.left"),sQuery(id+"F20.wireOp",EDGE,"E10.right")])],"isStart":true}),makeQuery(id+"F26.opExtrude","CAP_FACE",FACE,{"disambiguationData":[OSD([sQuery(id+"F25.wireOp",EDGE,"E12.bottom"),sQuery(id+"F25.wireOp",EDGE,"E12.top"),sQuery(id+"F25.wireOp",EDGE,"E12.left"),sQuery(id+"F25.wireOp",EDGE,"E12.right")])],"isStart":true})]});
            var sketch = newSketch(context, id + "F41", { "sketchPlane" : qUnion([Q0])});
            skLineSegment(sketch, "E27.bottom", {"start": v(-38.5, 5.05) * mm, "end": v(-36.9, 5.05) * mm});
            skLineSegment(sketch, "E27.top", {"start": v(-38.5, -5.05) * mm, "end": v(-36.9, -5.05) * mm});
            skLineSegment(sketch, "E27.left", {"start": v(-38.5, 5.05) * mm, "end": v(-38.5, -5.05) * mm});
            skLineSegment(sketch, "E27.right", {"start": v(-36.9, 5.05) * mm, "end": v(-36.9, -5.05) * mm});
            skLineSegment(sketch, "E28", {"start": v(-38.5, 0) * mm, "end": v(-36.9, 0) * mm, "construction": true});
            skLineSegment(sketch, "E29", {"start": v(0, 8.73) * mm, "end": v(0, 0) * mm, "construction": true});
            skLineSegment(sketch, "E30.MirrorCS", {"start": v(36.9, 5.05) * mm, "end": v(36.9, -5.05) * mm});
            skLineSegment(sketch, "E31.MirrorCS", {"start": v(38.5, -5.05) * mm, "end": v(36.9, -5.05) * mm});
            skLineSegment(sketch, "E32.MirrorCS", {"start": v(38.5, 5.05) * mm, "end": v(38.5, -5.05) * mm});
            skLineSegment(sketch, "E33.MirrorCS", {"start": v(38.5, 5.05) * mm, "end": v(36.9, 5.05) * mm});
            skLineSegment(sketch, "E34.bottom", {"start": v(-5.05, -82.5) * mm, "end": v(5.05, -82.5) * mm});
            skLineSegment(sketch, "E34.top", {"start": v(-5.05, -80.9) * mm, "end": v(5.05, -80.9) * mm});
            skLineSegment(sketch, "E34.left", {"start": v(-5.05, -82.5) * mm, "end": v(-5.05, -80.9) * mm});
            skLineSegment(sketch, "E34.right", {"start": v(5.05, -82.5) * mm, "end": v(5.05, -80.9) * mm});
            skLineSegment(sketch, "E35", {"start": v(0, -80.9) * mm, "end": v(0, -82.5) * mm, "construction": true});
            skSolve(sketch);
        }
        {
            var Q0;
            Q0=qSketchRegion(id+"F41",true);
            extrude(context, id + "F42", {"entities" : qUnion([Q0]), "operationType" : NewBodyOperationType.REMOVE, "endBound" : BoundingType.UP_TO_NEXT, "oppositeDirection" : true, "depth" : 25 * mm});
        }
        {
            var Q0;
            Q0=qCreatedBy(id+"F19.planeOp",FACE);
            var sketch = newSketch(context, id + "F43", { "sketchPlane" : qUnion([Q0])});
            skLineSegment(sketch, "E36", {"start": v(53, -12) * mm, "end": v(53, 12) * mm});
            skLineSegment(sketch, "E37", {"start": v(53, 12) * mm, "end": v(50, 12) * mm});
            skLineSegment(sketch, "E38", {"start": v(50, 12) * mm, "end": v(50, 5) * mm});
            skLineSegment(sketch, "E39", {"start": v(50, 5) * mm, "end": v(51.5, 5) * mm});
            skLineSegment(sketch, "E40", {"start": v(51.5, 5) * mm, "end": v(51.5, -5) * mm});
            skLineSegment(sketch, "E41", {"start": v(51.5, -5) * mm, "end": v(50, -5) * mm});
            skLineSegment(sketch, "E42", {"start": v(50, -5) * mm, "end": v(50, -12) * mm});
            skLineSegment(sketch, "E43", {"start": v(50, -12) * mm, "end": v(53, -12) * mm});
            skLineSegment(sketch, "E44", {"start": v(51.5, 0) * mm, "end": v(40.9, 0) * mm, "construction": true});
            skLineSegment(sketch, "E45", {"start": v(0, 0) * mm, "end": v(0, -18) * mm, "construction": true});
            skLineSegment(sketch, "E46.MirrorCS", {"start": v(-53, -12) * mm, "end": v(-53, 12) * mm});
            skLineSegment(sketch, "E47.MirrorCS", {"start": v(-53, 12) * mm, "end": v(-50, 12) * mm});
            skLineSegment(sketch, "E48.MirrorCS", {"start": v(-50, 12) * mm, "end": v(-50, 5) * mm});
            skLineSegment(sketch, "E49.MirrorCS", {"start": v(-50, 5) * mm, "end": v(-51.5, 5) * mm});
            skLineSegment(sketch, "E50.MirrorCS", {"start": v(-51.5, 5) * mm, "end": v(-51.5, -5) * mm});
            skLineSegment(sketch, "E51.MirrorCS", {"start": v(-51.5, -5) * mm, "end": v(-50, -5) * mm});
            skLineSegment(sketch, "E52.MirrorCS", {"start": v(-50, -5) * mm, "end": v(-50, -12) * mm});
            skLineSegment(sketch, "E53.MirrorCS", {"start": v(-50, -12) * mm, "end": v(-53, -12) * mm});
            skLineSegment(sketch, "E54", {"start": v(12, -97) * mm, "end": v(-12, -97) * mm});
            skLineSegment(sketch, "E55", {"start": v(-12, -97) * mm, "end": v(-12, -94) * mm});
            skLineSegment(sketch, "E56", {"start": v(-12, -94) * mm, "end": v(-5, -94) * mm});
            skLineSegment(sketch, "E57", {"start": v(-5, -94) * mm, "end": v(-5, -95.5) * mm});
            skLineSegment(sketch, "E58", {"start": v(-5, -95.5) * mm, "end": v(5, -95.5) * mm});
            skLineSegment(sketch, "E59", {"start": v(5, -95.5) * mm, "end": v(5, -94) * mm});
            skLineSegment(sketch, "E60", {"start": v(5, -94) * mm, "end": v(12, -94) * mm});
            skLineSegment(sketch, "E61", {"start": v(12, -94) * mm, "end": v(12, -97) * mm});
            skLineSegment(sketch, "E62", {"start": v(0, -95.5) * mm, "end": v(0, -78.2) * mm, "construction": true});
            skSolve(sketch);
        }
        {
            var Q0;
            Q0=qSketchRegion(id+"F43",true);
            extrude(context, id + "F44", {"entities" : qUnion([Q0]), "operationType" : NewBodyOperationType.REMOVE, "endBound" : BoundingType.UP_TO_NEXT, "oppositeDirection" : true, "depth" : 25 * mm});
        }
        {
            var Q0;
            {var subQ2=sQuery(id+"F35.wireOp",EDGE,"E22.bottom");var subQ3=sQuery(id+"F23.wireOp",EDGE,"E11.right");Q0=makeQuery(id+"F44.boolean.opBoolean","SPLIT",FACE,{"disambiguationData":[TD([makeQuery(id+"F24.opExtrude","SWEPT_FACE",FACE,{"disambiguationData":[OSD([subQ3])]})])],"derivedFrom":makeQuery(id+"F36.boolean.opBoolean","MERGE",FACE,{"derivedFrom":[makeQuery(id+"F24.opExtrude","CAP_FACE",FACE,{"disambiguationData":[OSD([sQuery(id+"F23.wireOp",EDGE,"E11.bottom"),sQuery(id+"F23.wireOp",EDGE,"E11.top"),sQuery(id+"F23.wireOp",EDGE,"E11.left"),subQ3])],"isStart":false}),makeQuery(id+"F36.opExtrude","SWEPT_FACE",FACE,{"disambiguationData":[OSD([subQ2])]}),makeQuery(id+"F36.opExtrude","SWEPT_FACE",FACE,{"disambiguationData":[OSD([sQuery(id+"F35.wireOp",EDGE,"E23.bottom")])]})]})});}
            var sketch = newSketch(context, id + "F45", { "sketchPlane" : qUnion([Q0])});
            skLineSegment(sketch, "E63.bottom", {"start": v(-6, 22.5) * mm, "end": v(6, 22.5) * mm});
            skLineSegment(sketch, "E63.top", {"start": v(-6, 20) * mm, "end": v(6, 20) * mm});
            skLineSegment(sketch, "E63.left", {"start": v(-6, 22.5) * mm, "end": v(-6, 20) * mm});
            skLineSegment(sketch, "E63.right", {"start": v(6, 22.5) * mm, "end": v(6, 20) * mm});
            skSolve(sketch);
        }
        {
            var Q0;
            Q0=qSketchRegion(id+"F45",true);
            extrude(context, id + "F46", {"entities" : qUnion([Q0]), "operationType" : NewBodyOperationType.ADD, "oppositeDirection" : true, "depth" : 3 * mm});
        }
    });
